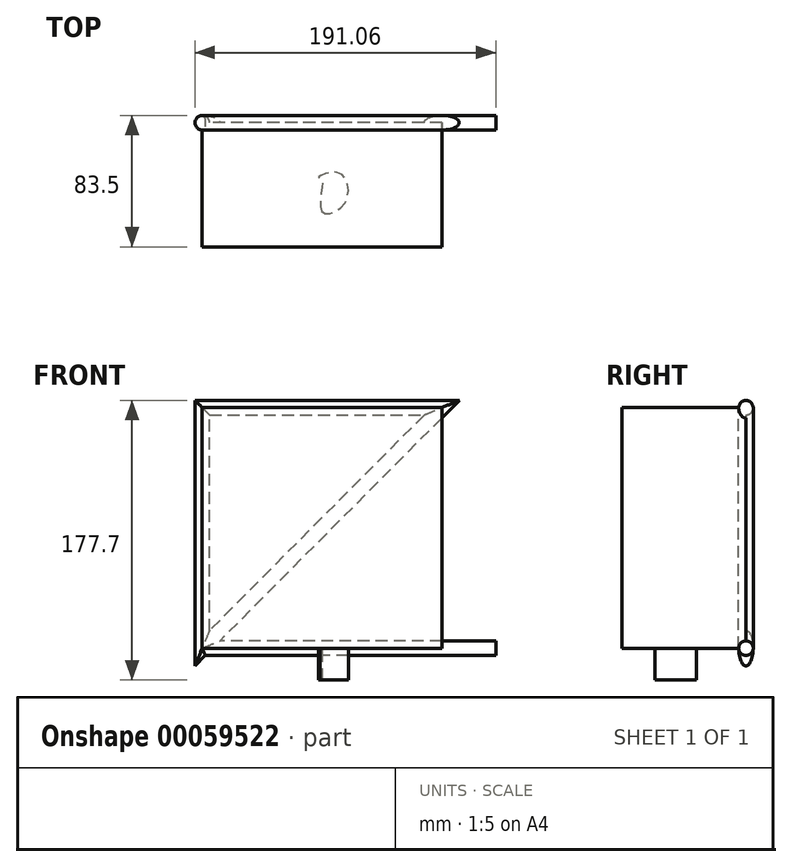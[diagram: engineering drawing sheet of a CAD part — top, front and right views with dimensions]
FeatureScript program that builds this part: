
annotation { "Feature Type Name" : "Feature", "Feature Type Description" : "" }
export const myFeature = defineFeature(function(context is Context, id is Id, definition is map)
    precondition{}
    {
        {
            var Q0;
            Q0=qCreatedBy(makeId("Top.planeOp"),FACE);
            var sketch = newSketch(context, id + "F0", { "sketchPlane" : qUnion([Q0])});
            skLineSegment(sketch, "E0", {"start": v(-75.9, 0) * mm, "end": v(-75.9, 56.17) * mm});
            skLineSegment(sketch, "E1", {"start": v(-75.9, 56.17) * mm, "end": v(76.24, 56.17) * mm});
            skLineSegment(sketch, "E2", {"start": v(76.24, 56.17) * mm, "end": v(76.24, -22.7) * mm});
            skLineSegment(sketch, "E3", {"start": v(76.24, -22.7) * mm, "end": v(-75.9, -22.7) * mm});
            skLineSegment(sketch, "E4", {"start": v(-75.9, -22.7) * mm, "end": v(-75.9, 0) * mm});
            skSolve(sketch);
        }
        {
            var Q0;
            Q0=makeQuery(id+"F0.imprint","IMPRINT",FACE,{"disambiguationData":[TD([[makeQuery(id+"F0.imprint","IMPRINT",EDGE,{"derivedFrom":sQuery(id+"F0.wireOp",EDGE,"E0")}),-1.0]])]});
            extrude(context, id + "F1", {"entities" : qUnion([Q0]), "depth" : 152.8 * mm});
        }
        {
            var Q0;
            Q0=makeQuery(id+"F1.opExtrude","SWEPT_FACE",FACE,{"disambiguationData":[OSD([sQuery(id+"F0.wireOp",EDGE,"E1")])]});
            var sketch = newSketch(context, id + "F2", { "sketchPlane" : qUnion([Q0])});
            skLineSegment(sketch, "E5", {"start": v(75.9, 0) * mm, "end": v(-76.24, 152.8) * mm});
            skLineSegment(sketch, "E6", {"start": v(-76.24, 152.8) * mm, "end": v(75.9, 152.8) * mm});
            skLineSegment(sketch, "E7", {"start": v(75.9, 152.8) * mm, "end": v(75.9, 0) * mm});
            skLineSegment(sketch, "E8", {"start": v(-76.24, 0) * mm, "end": v(75.9, 0) * mm});
            skLineSegment(sketch, "E9", {"start": v(-76.24, 152.8) * mm, "end": v(-76.24, 0) * mm});
            skSolve(sketch);
        }
        {
            var Q0;
            Q0=makeQuery(id+"F1.opExtrude","CAP_FACE",FACE,{"disambiguationData":[OSD([sQuery(id+"F0.wireOp",EDGE,"E0"),sQuery(id+"F0.wireOp",EDGE,"E1"),sQuery(id+"F0.wireOp",EDGE,"E2"),sQuery(id+"F0.wireOp",EDGE,"E3"),sQuery(id+"F0.wireOp",EDGE,"E4")])],"isStart":true});
            var sketch = newSketch(context, id + "F3", { "sketchPlane" : qUnion([Q0])});
            skCircle(sketch, "E10", {"center": v(-75.9, -56.17) * mm, "radius": 4.63 * mm});
            skSolve(sketch);
        }
        {
            var Q0;
            {var subQ0=sQuery(id+"F3.wireOp",EDGE,"E10");var subQ3=makeQuery(id+"F1.opExtrude","CAP_EDGE",EDGE,{"disambiguationData":[OSD([sQuery(id+"F0.wireOp",EDGE,"E1")])],"isStart":true});var subQ4=makeQuery(id+"F3.imprint","INTERSECT",VERTEX,{"derivedFrom":[subQ3,subQ0]});Q0=makeQuery(id+"F3.imprint","IMPRINT",FACE,{"disambiguationData":[TD([[makeQuery(id+"F3.imprint","IMPRINT",EDGE,{"disambiguationData":[TD([[subQ4,1.0]])],"derivedFrom":subQ0}),1.0]])]});}
            var Q1;
            Q1=sQuery(id+"F2.wireOp",EDGE,"E7");
            var Q2;
            Q2=sQuery(id+"F2.wireOp",EDGE,"E6");
            var Q3;
            Q3=sQuery(id+"F2.wireOp",EDGE,"E5");
            sweep(context, id + "F4", {"operationType" : NewBodyOperationType.ADD, "profiles" : qUnion([Q0]), "path" : qUnion([Q1, Q2, Q3])});
        }
        {
            var Q0;
            Q0=makeQuery(id+"F1.opExtrude","SWEPT_FACE",FACE,{"disambiguationData":[OSD([sQuery(id+"F0.wireOp",EDGE,"E2")])]});
            var sketch = newSketch(context, id + "F5", { "sketchPlane" : qUnion([Q0])});
            skCircle(sketch, "E11", {"center": v(56.17, 0) * mm, "radius": 4.63 * mm});
            skSolve(sketch);
        }
        {
            var Q0;
            Q0 = qSketchRegion(id + "F5", true);
            extrude(context, id + "F6", {"entities" : qUnion([Q0]), "operationType" : NewBodyOperationType.ADD, "depth" : 34.3 * mm});
        }
        {
            var Q0;
            Q0=makeQuery(id+"F6.opExtrude","CAP_FACE",FACE,{"disambiguationData":[OSD([sQuery(id+"F5.wireOp",EDGE,"E11")])],"isStart":true});
            var Q1;
            Q1=makeQuery(id+"F1.opExtrude","CAP_EDGE",EDGE,{"disambiguationData":[OSD([sQuery(id+"F0.wireOp",EDGE,"E1")])],"isStart":true});
            sweep(context, id + "F7", {"operationType" : NewBodyOperationType.ADD, "profiles" : qUnion([Q0]), "path" : qUnion([Q1])});
        }
        {
            var Q0;
            Q0=makeQuery(id+"F7.opSweep","CAP_FACE",FACE,{"disambiguationData":[OSD([sQuery(id+"F0.wireOp",EDGE,"E0"),sQuery(id+"F0.wireOp",EDGE,"E1"),sQuery(id+"F0.wireOp",EDGE,"E2"),sQuery(id+"F0.wireOp",EDGE,"E3"),sQuery(id+"F0.wireOp",EDGE,"E4"),sQuery(id+"F2.wireOp",EDGE,"E5"),sQuery(id+"F3.wireOp",EDGE,"E10"),sQuery(id+"F5.wireOp",EDGE,"E11")])],"isStart":false});
            extrude(context, id + "F8", {"entities" : qUnion([Q0]), "operationType" : NewBodyOperationType.ADD, "depth" : 6.18 * mm});
        }
        {
            var Q0;
            {var subQ1=makeQuery(id+"F1.opExtrude","CAP_EDGE",EDGE,{"disambiguationData":[OSD([sQuery(id+"F0.wireOp",EDGE,"E2")])],"isStart":true});Q0=makeQuery(id+"F3.imprint","IMPRINT",FACE,{"disambiguationData":[TD([[makeQuery(id+"F3.imprint","IMPRINT",EDGE,{"derivedFrom":subQ1}),1.0]])]});}
            var sketch = newSketch(context, id + "F9", { "sketchPlane" : qUnion([Q0])});
            skFitSpline(sketch, "E12", {"points": [v(0, 0) * mm, v(14.65, -5.07) * mm, v(10.78, -24.31) * mm, v(-2.03, -21.5) * mm, v(0, -20.2) * mm, v(0, 0) * mm]});
            skSolve(sketch);
        }
        {
            var Q0;
            Q0=makeQuery(id+"F9.imprint","IMPRINT",FACE,{"disambiguationData":[TD([[makeQuery(id+"F9.imprint","IMPRINT",EDGE,{"derivedFrom":sQuery(id+"F9.wireOp",EDGE,"E12")}),-1.0]])]});
            extrude(context, id + "F10", {"entities" : qUnion([Q0]), "operationType" : NewBodyOperationType.ADD, "depth" : 20.28 * mm});
        }
    });
